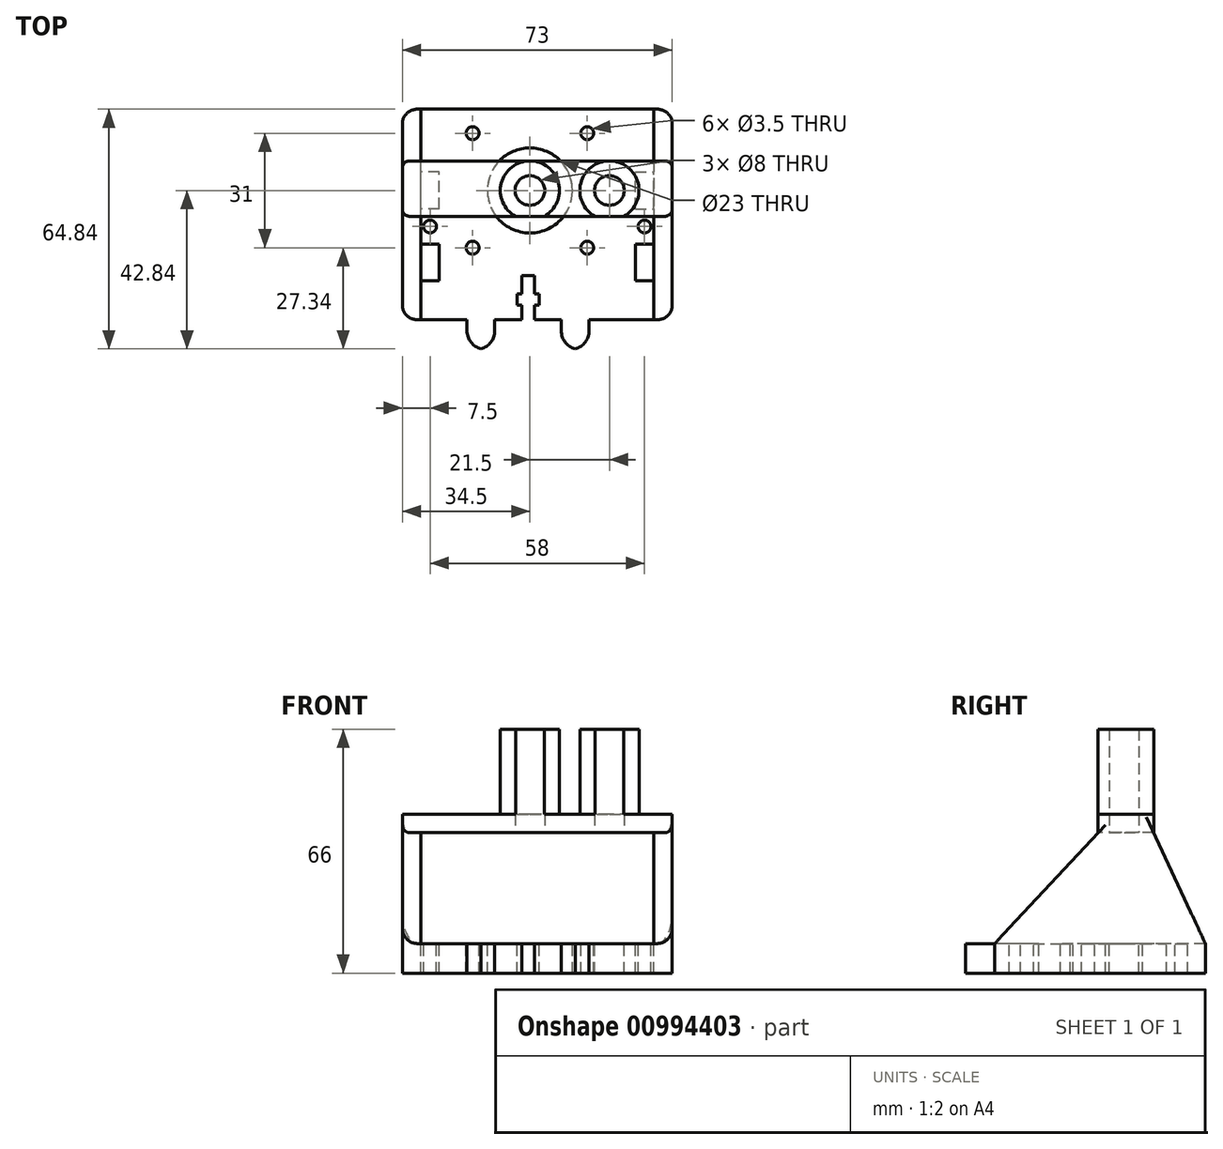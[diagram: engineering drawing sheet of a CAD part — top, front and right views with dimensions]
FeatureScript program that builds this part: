
annotation { "Feature Type Name" : "Feature", "Feature Type Description" : "" }
export const myFeature = defineFeature(function(context is Context, id is Id, definition is map)
    precondition{}
    {
        {
            var Q0;
            Q0=qCreatedBy(makeId("Top.planeOp"),FACE);
            var sketch = newSketch(context, id + "F0", { "sketchPlane" : qUnion([Q0])});
            skLineSegment(sketch, "E0.bottom", {"start": v(0, 0) * mm, "end": v(73, 0) * mm});
            skLineSegment(sketch, "E0.top", {"start": v(0, 57) * mm, "end": v(73, 57) * mm});
            skLineSegment(sketch, "E0.left", {"start": v(0, 0) * mm, "end": v(0, 57) * mm});
            skLineSegment(sketch, "E0.right", {"start": v(73, 0) * mm, "end": v(73, 57) * mm});
            skCircle(sketch, "E1", {"center": v(38.5, 35) * mm, "radius": 11.5 * mm});
            skCircle(sketch, "E2", {"center": v(17, 35) * mm, "radius": 4 * mm});
            skLineSegment(sketch, "E3.bottom", {"start": v(10, 10.5) * mm, "end": v(5, 10.5) * mm});
            skLineSegment(sketch, "E3.top", {"start": v(10, 20.5) * mm, "end": v(5, 20.5) * mm});
            skLineSegment(sketch, "E3.left", {"start": v(10, 10.5) * mm, "end": v(10, 20.5) * mm});
            skLineSegment(sketch, "E3.right", {"start": v(5, 10.5) * mm, "end": v(5, 20.5) * mm});
            skLineSegment(sketch, "E4.bottom", {"start": v(10, 30) * mm, "end": v(5, 30) * mm});
            skLineSegment(sketch, "E4.top", {"start": v(10, 40) * mm, "end": v(5, 40) * mm});
            skLineSegment(sketch, "E4.left", {"start": v(10, 30) * mm, "end": v(10, 40) * mm});
            skLineSegment(sketch, "E4.right", {"start": v(5, 30) * mm, "end": v(5, 40) * mm});
            skLineSegment(sketch, "E5.bottom", {"start": v(68, 10.5) * mm, "end": v(63, 10.5) * mm});
            skLineSegment(sketch, "E5.top", {"start": v(68, 20.5) * mm, "end": v(63, 20.5) * mm});
            skLineSegment(sketch, "E5.left", {"start": v(68, 10.5) * mm, "end": v(68, 20.5) * mm});
            skLineSegment(sketch, "E5.right", {"start": v(63, 10.5) * mm, "end": v(63, 20.5) * mm});
            skLineSegment(sketch, "E6.bottom", {"start": v(63, 30) * mm, "end": v(68, 30) * mm});
            skLineSegment(sketch, "E6.top", {"start": v(63, 40) * mm, "end": v(68, 40) * mm});
            skLineSegment(sketch, "E6.left", {"start": v(63, 30) * mm, "end": v(63, 40) * mm});
            skLineSegment(sketch, "E6.right", {"start": v(68, 30) * mm, "end": v(68, 40) * mm});
            skCircle(sketch, "E7", {"center": v(23, 50.5) * mm, "radius": 1.75 * mm});
            skCircle(sketch, "E8", {"center": v(54, 50.5) * mm, "radius": 1.75 * mm});
            skCircle(sketch, "E9", {"center": v(54, 19.5) * mm, "radius": 1.75 * mm});
            skCircle(sketch, "E10", {"center": v(23, 19.5) * mm, "radius": 1.75 * mm});
            skLineSegment(sketch, "E11", {"start": v(23, 50.5) * mm, "end": v(54, 19.5) * mm, "construction": true});
            skLineSegment(sketch, "E12", {"start": v(22.5, 0) * mm, "end": v(22.5, -8) * mm});
            skLineSegment(sketch, "E13", {"start": v(22.5, -8) * mm, "end": v(30, -8) * mm});
            skLineSegment(sketch, "E14", {"start": v(30, -8) * mm, "end": v(30, 0) * mm});
            skLineSegment(sketch, "E15", {"start": v(48, 0) * mm, "end": v(48, -8) * mm});
            skLineSegment(sketch, "E16", {"start": v(48, -8) * mm, "end": v(55.5, -8) * mm});
            skLineSegment(sketch, "E17", {"start": v(55.5, -8) * mm, "end": v(55.5, 0) * mm});
            skLineSegment(sketch, "E18", {"start": v(37.25, 0) * mm, "end": v(37.25, 12) * mm});
            skLineSegment(sketch, "E19", {"start": v(37.25, 12) * mm, "end": v(40.75, 12) * mm});
            skLineSegment(sketch, "E20", {"start": v(40.75, 12) * mm, "end": v(40.75, 0) * mm});
            skLineSegment(sketch, "E21.bottom", {"start": v(36, 7) * mm, "end": v(42, 7) * mm});
            skLineSegment(sketch, "E21.top", {"start": v(36, 4) * mm, "end": v(42, 4) * mm});
            skLineSegment(sketch, "E21.left", {"start": v(36, 7) * mm, "end": v(36, 4) * mm});
            skLineSegment(sketch, "E21.right", {"start": v(42, 7) * mm, "end": v(42, 4) * mm});
            skLineSegment(sketch, "E22", {"start": v(5, 30) * mm, "end": v(10, 20.5) * mm, "construction": true});
            skLineSegment(sketch, "E23", {"start": v(63, 30) * mm, "end": v(68, 20.5) * mm, "construction": true});
            skCircle(sketch, "E24", {"center": v(7.5, 25.25) * mm, "radius": 1.75 * mm});
            skCircle(sketch, "E25", {"center": v(65.5, 25.25) * mm, "radius": 1.75 * mm});
            skSolve(sketch);
        }
        {
            var Q0;
            Q0=makeQuery(id+"F0.imprint","IMPRINT",FACE,{"disambiguationData":[TD([[makeQuery(id+"F0.imprint","IMPRINT",EDGE,{"derivedFrom":sQuery(id+"F0.wireOp",EDGE,"E0.top")}),-1.0]])]});
            var Q1;
            {var subQ0=sQuery(id+"F0.wireOp",EDGE,"E15");Q1=makeQuery(id+"F0.imprint","IMPRINT",FACE,{"disambiguationData":[TD([[makeQuery(id+"F0.imprint","IMPRINT",EDGE,{"derivedFrom":subQ0}),1.0]])]});}
            var Q2;
            {var subQ0=sQuery(id+"F0.wireOp",EDGE,"E12");Q2=makeQuery(id+"F0.imprint","IMPRINT",FACE,{"disambiguationData":[TD([[makeQuery(id+"F0.imprint","IMPRINT",EDGE,{"derivedFrom":subQ0}),1.0]])]});}
            extrude(context, id + "F1", {"entities" : qUnion([Q0, Q1, Q2]), "oppositeDirection" : true, "depth" : 8 * mm, "offsetDistance" : 25 * mm});
        }
        {
            var Q0;
            Q0=qCreatedBy(makeId("Top.planeOp"),FACE);
            var sketch = newSketch(context, id + "F2", { "sketchPlane" : qUnion([Q0])});
            skLineSegment(sketch, "E26.0.0", {"start": v(0, 0) * mm, "end": v(22.5, 0) * mm});
            skLineSegment(sketch, "E26.0.1", {"start": v(22.5, 0) * mm, "end": v(22.5, -8) * mm});
            skLineSegment(sketch, "E26.0.2", {"start": v(22.5, -8) * mm, "end": v(30, -8) * mm});
            skLineSegment(sketch, "E26.0.3", {"start": v(30, -8) * mm, "end": v(30, 0) * mm});
            skLineSegment(sketch, "E26.0.4", {"start": v(30, 0) * mm, "end": v(37.25, 0) * mm});
            skLineSegment(sketch, "E26.0.5", {"start": v(37.25, 0) * mm, "end": v(37.25, 4) * mm});
            skLineSegment(sketch, "E26.0.6", {"start": v(37.25, 4) * mm, "end": v(36, 4) * mm});
            skLineSegment(sketch, "E26.0.7", {"start": v(36, 4) * mm, "end": v(36, 7) * mm});
            skLineSegment(sketch, "E26.0.8", {"start": v(36, 7) * mm, "end": v(37.25, 7) * mm});
            skLineSegment(sketch, "E26.0.9", {"start": v(37.25, 7) * mm, "end": v(37.25, 12) * mm});
            skLineSegment(sketch, "E26.0.10", {"start": v(37.25, 12) * mm, "end": v(40.75, 12) * mm});
            skLineSegment(sketch, "E26.0.11", {"start": v(40.75, 12) * mm, "end": v(40.75, 7) * mm});
            skLineSegment(sketch, "E26.0.12", {"start": v(40.75, 7) * mm, "end": v(42, 7) * mm});
            skLineSegment(sketch, "E26.0.13", {"start": v(42, 7) * mm, "end": v(42, 4) * mm});
            skLineSegment(sketch, "E26.0.14", {"start": v(42, 4) * mm, "end": v(40.75, 4) * mm});
            skLineSegment(sketch, "E26.0.15", {"start": v(40.75, 4) * mm, "end": v(40.75, 0) * mm});
            skLineSegment(sketch, "E26.0.16", {"start": v(40.75, 0) * mm, "end": v(48, 0) * mm});
            skLineSegment(sketch, "E26.0.17", {"start": v(48, 0) * mm, "end": v(48, -8) * mm});
            skLineSegment(sketch, "E26.0.18", {"start": v(48, -8) * mm, "end": v(55.5, -8) * mm});
            skLineSegment(sketch, "E26.0.19", {"start": v(55.5, -8) * mm, "end": v(55.5, 0) * mm});
            skLineSegment(sketch, "E26.0.20", {"start": v(55.5, 0) * mm, "end": v(73, 0) * mm});
            skLineSegment(sketch, "E26.0.21", {"start": v(73, 0) * mm, "end": v(73, 57) * mm});
            skLineSegment(sketch, "E26.0.22", {"start": v(73, 57) * mm, "end": v(0, 57) * mm});
            skLineSegment(sketch, "E26.0.23", {"start": v(0, 57) * mm, "end": v(0, 0) * mm});
            skLineSegment(sketch, "E27.0.0", {"start": v(5, 30) * mm, "end": v(10, 30) * mm});
            skLineSegment(sketch, "E27.0.1", {"start": v(10, 30) * mm, "end": v(10, 40) * mm});
            skLineSegment(sketch, "E27.0.2", {"start": v(10, 40) * mm, "end": v(5, 40) * mm});
            skLineSegment(sketch, "E27.0.3", {"start": v(5, 40) * mm, "end": v(5, 30) * mm});
            skLineSegment(sketch, "E28.0.0", {"start": v(5, 10.5) * mm, "end": v(10, 10.5) * mm});
            skLineSegment(sketch, "E28.0.1", {"start": v(10, 10.5) * mm, "end": v(10, 20.5) * mm});
            skLineSegment(sketch, "E28.0.2", {"start": v(10, 20.5) * mm, "end": v(5, 20.5) * mm});
            skLineSegment(sketch, "E28.0.3", {"start": v(5, 20.5) * mm, "end": v(5, 10.5) * mm});
            skCircle(sketch, "E29.0.0", {"center": v(7.5, 25.25) * mm, "radius": 1.75 * mm});
            skLineSegment(sketch, "E30.0.0", {"start": v(63, 10.5) * mm, "end": v(68, 10.5) * mm});
            skLineSegment(sketch, "E30.0.1", {"start": v(68, 10.5) * mm, "end": v(68, 20.5) * mm});
            skLineSegment(sketch, "E30.0.2", {"start": v(68, 20.5) * mm, "end": v(63, 20.5) * mm});
            skLineSegment(sketch, "E30.0.3", {"start": v(63, 20.5) * mm, "end": v(63, 10.5) * mm});
            skCircle(sketch, "E31.0.0", {"center": v(65.5, 25.25) * mm, "radius": 1.75 * mm});
            skLineSegment(sketch, "E32.0.0", {"start": v(63, 40) * mm, "end": v(63, 30) * mm});
            skLineSegment(sketch, "E32.0.1", {"start": v(63, 30) * mm, "end": v(68, 30) * mm});
            skLineSegment(sketch, "E32.0.2", {"start": v(68, 30) * mm, "end": v(68, 40) * mm});
            skLineSegment(sketch, "E32.0.3", {"start": v(68, 40) * mm, "end": v(63, 40) * mm});
            skPoint(sketch, "E33.0", {"position": v(17, 35) * mm});
            skLineSegment(sketch, "E34", {"start": v(5, 57) * mm, "end": v(5, 0) * mm});
            skLineSegment(sketch, "E35", {"start": v(68, 0) * mm, "end": v(68, 57) * mm});
            skSolve(sketch);
        }
        {
            var Q0;
            {var subQ0=sQuery(id+"F2.wireOp",EDGE,"E26.0.23");Q0=makeQuery(id+"F2.imprint","IMPRINT",FACE,{"disambiguationData":[TD([[makeQuery(id+"F2.imprint","IMPRINT",EDGE,{"derivedFrom":subQ0}),1.0]])]});}
            var Q1;
            {var subQ1=sQuery(id+"F2.wireOp",EDGE,"E26.0.21");Q1=makeQuery(id+"F2.imprint","IMPRINT",FACE,{"disambiguationData":[TD([[makeQuery(id+"F2.imprint","IMPRINT",EDGE,{"derivedFrom":subQ1}),1.0]])]});}
            extrude(context, id + "F3", {"entities" : qUnion([Q0, Q1]), "operationType" : NewBodyOperationType.ADD, "depth" : 30 * mm, "offsetDistance" : 25 * mm});
        }
        {
            var Q0;
            Q0=makeQuery(id+"F3.opExtrude","CAP_FACE",FACE,{"disambiguationData":[OSD([sQuery(id+"F2.wireOp",EDGE,"E26.0.0"),sQuery(id+"F2.wireOp",EDGE,"E26.0.22"),sQuery(id+"F2.wireOp",EDGE,"E26.0.23"),sQuery(id+"F2.wireOp",EDGE,"E27.0.3"),sQuery(id+"F2.wireOp",EDGE,"E28.0.3"),sQuery(id+"F2.wireOp",EDGE,"E34")])],"isStart":false});
            var sketch = newSketch(context, id + "F4", { "sketchPlane" : qUnion([Q0])});
            skLineSegment(sketch, "E36.0.0", {"start": v(0, 57) * mm, "end": v(0, 0) * mm});
            skLineSegment(sketch, "E36.0.1", {"start": v(0, 0) * mm, "end": v(5, 0) * mm});
            skLineSegment(sketch, "E36.0.2", {"start": v(5, 0) * mm, "end": v(5, 57) * mm});
            skLineSegment(sketch, "E36.0.3", {"start": v(5, 57) * mm, "end": v(0, 57) * mm});
            skLineSegment(sketch, "E37.0.0", {"start": v(68, 57) * mm, "end": v(68, 0) * mm});
            skLineSegment(sketch, "E37.0.1", {"start": v(68, 0) * mm, "end": v(73, 0) * mm});
            skLineSegment(sketch, "E37.0.2", {"start": v(73, 0) * mm, "end": v(73, 57) * mm});
            skLineSegment(sketch, "E37.0.3", {"start": v(73, 57) * mm, "end": v(68, 57) * mm});
            skCircle(sketch, "E38.0", {"center": v(17, 35) * mm, "radius": 4 * mm});
            skLineSegment(sketch, "E39", {"start": v(0, 43) * mm, "end": v(73, 43) * mm});
            skLineSegment(sketch, "E40", {"start": v(73, 28) * mm, "end": v(0, 28) * mm});
            skPoint(sketch, "E41.0", {"position": v(38.5, 35) * mm});
            skCircle(sketch, "E42", {"center": v(38.5, 35) * mm, "radius": 4 * mm});
            skSolve(sketch);
        }
        {
            var Q0;
            {var subQ0=sQuery(id+"F4.wireOp",EDGE,"E40");var subQ1=sQuery(id+"F4.wireOp",EDGE,"E36.0.0");var subQ2=makeQuery(id+"F4.imprint","INTERSECT",VERTEX,{"derivedFrom":[subQ1,subQ0]});Q0=makeQuery(id+"F4.imprint","IMPRINT",FACE,{"disambiguationData":[TD([[makeQuery(id+"F4.imprint","IMPRINT",EDGE,{"disambiguationData":[TD([[subQ2,1.0]])],"derivedFrom":subQ1}),1.0]])]});}
            var Q1;
            Q1=makeQuery(id+"F4.imprint","IMPRINT",FACE,{"disambiguationData":[TD([[makeQuery(id+"F4.imprint","IMPRINT",EDGE,{"derivedFrom":sQuery(id+"F4.wireOp",EDGE,"E38.0")}),-1.0]])]});
            var Q2;
            {var subQ0=sQuery(id+"F4.wireOp",EDGE,"E40");var subQ1=sQuery(id+"F4.wireOp",EDGE,"E37.0.0");var subQ2=makeQuery(id+"F4.imprint","INTERSECT",VERTEX,{"derivedFrom":[subQ1,subQ0]});Q2=makeQuery(id+"F4.imprint","IMPRINT",FACE,{"disambiguationData":[TD([[makeQuery(id+"F4.imprint","IMPRINT",EDGE,{"disambiguationData":[TD([[subQ2,1.0]])],"derivedFrom":subQ1}),1.0]])]});}
            extrude(context, id + "F5", {"entities" : qUnion([Q0, Q1, Q2]), "operationType" : NewBodyOperationType.ADD, "depth" : 5 * mm, "offsetDistance" : 25 * mm});
        }
        {
            var Q0;
            Q0=makeQuery(id+"F5.opExtrude","CAP_FACE",FACE,{"disambiguationData":[OSD([sQuery(id+"F4.wireOp",EDGE,"E36.0.0"),sQuery(id+"F4.wireOp",EDGE,"E37.0.2"),sQuery(id+"F4.wireOp",EDGE,"E38.0"),sQuery(id+"F4.wireOp",EDGE,"E39"),sQuery(id+"F4.wireOp",EDGE,"E40"),sQuery(id+"F4.wireOp",EDGE,"E42")])],"isStart":false});
            var sketch = newSketch(context, id + "F6", { "sketchPlane" : qUnion([Q0])});
            skLineSegment(sketch, "E43.0.0", {"start": v(73, 43) * mm, "end": v(0, 43) * mm});
            skLineSegment(sketch, "E43.0.1", {"start": v(0, 43) * mm, "end": v(0, 28) * mm});
            skLineSegment(sketch, "E43.0.2", {"start": v(0, 28) * mm, "end": v(73, 28) * mm});
            skLineSegment(sketch, "E43.0.3", {"start": v(73, 28) * mm, "end": v(73, 43) * mm});
            skCircle(sketch, "E44.0.0", {"center": v(17, 35) * mm, "radius": 4 * mm});
            skCircle(sketch, "E45.0", {"center": v(38.5, 35) * mm, "radius": 4 * mm});
            skCircle(sketch, "E46", {"center": v(17, 35) * mm, "radius": 8 * mm});
            skCircle(sketch, "E47", {"center": v(38.5, 35) * mm, "radius": 8 * mm});
            skSolve(sketch);
        }
        {
            var Q0;
            Q0=makeQuery(id+"F6.imprint","IMPRINT",FACE,{"disambiguationData":[TD([[makeQuery(id+"F6.imprint","IMPRINT",EDGE,{"derivedFrom":sQuery(id+"F6.wireOp",EDGE,"E44.0.0")}),-1.0]])]});
            var Q1;
            Q1=makeQuery(id+"F6.imprint","IMPRINT",FACE,{"disambiguationData":[TD([[makeQuery(id+"F6.imprint","IMPRINT",EDGE,{"derivedFrom":sQuery(id+"F6.wireOp",EDGE,"E45.0")}),-1.0]])]});
            extrude(context, id + "F7", {"entities" : qUnion([Q0, Q1]), "operationType" : NewBodyOperationType.ADD, "depth" : 23 * mm, "offsetDistance" : 25 * mm});
        }
        {
            var Q0;
            Q0=makeQuery(id+"F5.boolean.opBoolean","MERGE",FACE,{"derivedFrom":[makeQuery(id+"F3.boolean.opBoolean","MERGE",FACE,{"derivedFrom":[makeQuery(id+"F1.opExtrude","SWEPT_FACE",FACE,{"disambiguationData":[OSD([sQuery(id+"F0.wireOp",EDGE,"E0.left")])]}),makeQuery(id+"F3.opExtrude","SWEPT_FACE",FACE,{"disambiguationData":[OSD([sQuery(id+"F2.wireOp",EDGE,"E26.0.23")])]})]}),makeQuery(id+"F5.opExtrude","SWEPT_FACE",FACE,{"disambiguationData":[OSD([sQuery(id+"F4.wireOp",EDGE,"E36.0.0")])]})]});
            var sketch = newSketch(context, id + "F8", { "sketchPlane" : qUnion([Q0])});
            skPoint(sketch, "E48.0", {"position": v(-28, 30) * mm});
            skPoint(sketch, "E49.0", {"position": v(-57, 0) * mm});
            skPoint(sketch, "E50.0", {"position": v(-43, 30) * mm});
            skLineSegment(sketch, "E51", {"start": v(-28, 30) * mm, "end": v(0, 0) * mm});
            skLineSegment(sketch, "E52", {"start": v(-43, 30) * mm, "end": v(-57, 0) * mm});
            skSolve(sketch);
        }
        {
            var Q0;
            {var subQ0=sQuery(id+"F8.wireOp",EDGE,"E52");Q0=makeQuery(id+"F8.imprint","IMPRINT",FACE,{"disambiguationData":[TD([[makeQuery(id+"F8.imprint","IMPRINT",EDGE,{"derivedFrom":subQ0}),-1.0]])]});}
            var Q1;
            {var subQ0=sQuery(id+"F8.wireOp",EDGE,"E51");Q1=makeQuery(id+"F8.imprint","IMPRINT",FACE,{"disambiguationData":[TD([[makeQuery(id+"F8.imprint","IMPRINT",EDGE,{"derivedFrom":subQ0}),1.0]])]});}
            extrude(context, id + "F9", {"entities" : qUnion([Q0, Q1]), "operationType" : NewBodyOperationType.REMOVE, "oppositeDirection" : true, "depth" : 73 * mm, "offsetDistance" : 25 * mm});
        }
        {
            var Q0;
            Q0=makeQuery(id+"F3.boolean.opBoolean","MERGE",EDGE,{"derivedFrom":[makeQuery(id+"F1.opExtrude","SWEPT_EDGE",EDGE,{"disambiguationData":[OSD([sQuery(id+"F0.wireOp",EDGE,"E0.top"),sQuery(id+"F0.wireOp",EDGE,"E0.left")])]}),makeQuery(id+"F3.opExtrude","SWEPT_EDGE",EDGE,{"disambiguationData":[OSD([sQuery(id+"F2.wireOp",EDGE,"E26.0.22"),sQuery(id+"F2.wireOp",EDGE,"E26.0.23")])]})]});
            var Q1;
            Q1=makeQuery(id+"F3.boolean.opBoolean","MERGE",EDGE,{"derivedFrom":[makeQuery(id+"F1.opExtrude","SWEPT_EDGE",EDGE,{"disambiguationData":[OSD([sQuery(id+"F0.wireOp",EDGE,"E0.top"),sQuery(id+"F0.wireOp",EDGE,"E0.right")])]}),makeQuery(id+"F3.opExtrude","SWEPT_EDGE",EDGE,{"disambiguationData":[OSD([sQuery(id+"F2.wireOp",EDGE,"E26.0.21"),sQuery(id+"F2.wireOp",EDGE,"E26.0.22")])]})]});
            var Q2;
            Q2=makeQuery(id+"F3.boolean.opBoolean","MERGE",EDGE,{"derivedFrom":[makeQuery(id+"F1.opExtrude","SWEPT_EDGE",EDGE,{"disambiguationData":[OSD([sQuery(id+"F0.wireOp",EDGE,"E0.bottom"),sQuery(id+"F0.wireOp",EDGE,"E0.left")])]}),makeQuery(id+"F3.opExtrude","SWEPT_EDGE",EDGE,{"disambiguationData":[OSD([sQuery(id+"F2.wireOp",EDGE,"E26.0.0"),sQuery(id+"F2.wireOp",EDGE,"E26.0.23")])]})]});
            var Q3;
            Q3=makeQuery(id+"F3.boolean.opBoolean","MERGE",EDGE,{"derivedFrom":[makeQuery(id+"F1.opExtrude","SWEPT_EDGE",EDGE,{"disambiguationData":[OSD([sQuery(id+"F0.wireOp",EDGE,"E0.bottom"),sQuery(id+"F0.wireOp",EDGE,"E0.right")])]}),makeQuery(id+"F3.opExtrude","SWEPT_EDGE",EDGE,{"disambiguationData":[OSD([sQuery(id+"F2.wireOp",EDGE,"E26.0.20"),sQuery(id+"F2.wireOp",EDGE,"E26.0.21")])]})]});
            fillet(context, id + "F10", {"entities" : qUnion([Q0, Q1, Q2, Q3]), "tangentPropagation" : true, "radius" : 4 * mm, "defaultsChanged" : true, "vertexSettings" : [], "allowEdgeOverflow" : false});
        }
        {
            var Q0;
            Q0=makeQuery(id+"F5.opExtrude","SWEPT_EDGE",EDGE,{"disambiguationData":[OSD([sQuery(id+"F4.wireOp",EDGE,"E37.0.2"),sQuery(id+"F4.wireOp",EDGE,"E40")])]});
            var Q1;
            Q1=makeQuery(id+"F5.opExtrude","SWEPT_EDGE",EDGE,{"disambiguationData":[OSD([sQuery(id+"F4.wireOp",EDGE,"E36.0.0"),sQuery(id+"F4.wireOp",EDGE,"E40")])]});
            var Q2;
            Q2=makeQuery(id+"F5.opExtrude","SWEPT_EDGE",EDGE,{"disambiguationData":[OSD([sQuery(id+"F4.wireOp",EDGE,"E36.0.0"),sQuery(id+"F4.wireOp",EDGE,"E39")])]});
            var Q3;
            Q3=makeQuery(id+"F5.opExtrude","SWEPT_EDGE",EDGE,{"disambiguationData":[OSD([sQuery(id+"F4.wireOp",EDGE,"E37.0.2"),sQuery(id+"F4.wireOp",EDGE,"E39")])]});
            fillet(context, id + "F11", {"entities" : qUnion([Q0, Q1, Q2, Q3]), "tangentPropagation" : true, "radius" : 2 * mm, "defaultsChanged" : true, "vertexSettings" : [], "allowEdgeOverflow" : false});
        }
        {
            var Q0;
            Q0=makeQuery(id+"F1.opExtrude","SWEPT_EDGE",EDGE,{"disambiguationData":[OSD([sQuery(id+"F0.wireOp",EDGE,"E13"),sQuery(id+"F0.wireOp",EDGE,"E14")])]});
            var Q1;
            Q1=makeQuery(id+"F1.opExtrude","SWEPT_EDGE",EDGE,{"disambiguationData":[OSD([sQuery(id+"F0.wireOp",EDGE,"E12"),sQuery(id+"F0.wireOp",EDGE,"E13")])]});
            var Q2;
            Q2=makeQuery(id+"F1.opExtrude","SWEPT_EDGE",EDGE,{"disambiguationData":[OSD([sQuery(id+"F0.wireOp",EDGE,"E16"),sQuery(id+"F0.wireOp",EDGE,"E17")])]});
            var Q3;
            Q3=makeQuery(id+"F1.opExtrude","SWEPT_EDGE",EDGE,{"disambiguationData":[OSD([sQuery(id+"F0.wireOp",EDGE,"E15"),sQuery(id+"F0.wireOp",EDGE,"E16")])]});
            fillet(context, id + "F12", {"entities" : qUnion([Q0, Q1, Q2, Q3]), "tangentPropagation" : true, "radius" : 5 * mm, "defaultsChanged" : false, "vertexSettings" : [], "allowEdgeOverflow" : false});
        }
        {
            var Q0;
            Q0=makeQuery(id+"F1.opExtrude","SWEPT_BODY",BODY,{"disambiguationData":[OSD([sQuery(id+"F0.wireOp",EDGE,"E0.bottom"),sQuery(id+"F0.wireOp",EDGE,"E0.top"),sQuery(id+"F0.wireOp",EDGE,"E0.left"),sQuery(id+"F0.wireOp",EDGE,"E0.right"),sQuery(id+"F0.wireOp",EDGE,"E1"),sQuery(id+"F0.wireOp",EDGE,"E2"),sQuery(id+"F0.wireOp",EDGE,"E3.bottom"),sQuery(id+"F0.wireOp",EDGE,"E3.top"),sQuery(id+"F0.wireOp",EDGE,"E3.left"),sQuery(id+"F0.wireOp",EDGE,"E3.right"),sQuery(id+"F0.wireOp",EDGE,"E4.bottom"),sQuery(id+"F0.wireOp",EDGE,"E4.top"),sQuery(id+"F0.wireOp",EDGE,"E4.left"),sQuery(id+"F0.wireOp",EDGE,"E4.right"),sQuery(id+"F0.wireOp",EDGE,"E5.bottom"),sQuery(id+"F0.wireOp",EDGE,"E5.top"),sQuery(id+"F0.wireOp",EDGE,"E5.left"),sQuery(id+"F0.wireOp",EDGE,"E5.right"),sQuery(id+"F0.wireOp",EDGE,"E6.bottom"),sQuery(id+"F0.wireOp",EDGE,"E6.top"),sQuery(id+"F0.wireOp",EDGE,"E6.left"),sQuery(id+"F0.wireOp",EDGE,"E6.right"),sQuery(id+"F0.wireOp",EDGE,"E7"),sQuery(id+"F0.wireOp",EDGE,"E8"),sQuery(id+"F0.wireOp",EDGE,"E9"),sQuery(id+"F0.wireOp",EDGE,"E10"),sQuery(id+"F0.wireOp",EDGE,"E12"),sQuery(id+"F0.wireOp",EDGE,"E13"),sQuery(id+"F0.wireOp",EDGE,"E14"),sQuery(id+"F0.wireOp",EDGE,"E15"),sQuery(id+"F0.wireOp",EDGE,"E16"),sQuery(id+"F0.wireOp",EDGE,"E17"),sQuery(id+"F0.wireOp",EDGE,"E18"),sQuery(id+"F0.wireOp",EDGE,"E19"),sQuery(id+"F0.wireOp",EDGE,"E20"),sQuery(id+"F0.wireOp",EDGE,"E21.bottom"),sQuery(id+"F0.wireOp",EDGE,"E21.top"),sQuery(id+"F0.wireOp",EDGE,"E21.left"),sQuery(id+"F0.wireOp",EDGE,"E21.right"),sQuery(id+"F0.wireOp",EDGE,"E24"),sQuery(id+"F0.wireOp",EDGE,"E25")])]});
            var Q1;
            Q1=makeQuery(id+"F5.boolean.opBoolean","MERGE",FACE,{"derivedFrom":[makeQuery(id+"F3.boolean.opBoolean","MERGE",FACE,{"derivedFrom":[makeQuery(id+"F1.opExtrude","SWEPT_FACE",FACE,{"disambiguationData":[OSD([sQuery(id+"F0.wireOp",EDGE,"E0.left")])]}),makeQuery(id+"F3.opExtrude","SWEPT_FACE",FACE,{"disambiguationData":[OSD([sQuery(id+"F2.wireOp",EDGE,"E26.0.23")])]})]}),makeQuery(id+"F5.opExtrude","SWEPT_FACE",FACE,{"disambiguationData":[OSD([sQuery(id+"F4.wireOp",EDGE,"E36.0.0")])]})]});
            mirror(context, id + "F13", {"entities" : qUnion([Q0]), "mirrorPlane" : qUnion([Q1])});
        }
        {
            var Q0;
            Q0=makeQuery(id+"F1.opExtrude","SWEPT_BODY",BODY,{"disambiguationData":[OSD([sQuery(id+"F0.wireOp",EDGE,"E0.bottom"),sQuery(id+"F0.wireOp",EDGE,"E0.top"),sQuery(id+"F0.wireOp",EDGE,"E0.left"),sQuery(id+"F0.wireOp",EDGE,"E0.right"),sQuery(id+"F0.wireOp",EDGE,"E1"),sQuery(id+"F0.wireOp",EDGE,"E2"),sQuery(id+"F0.wireOp",EDGE,"E3.bottom"),sQuery(id+"F0.wireOp",EDGE,"E3.top"),sQuery(id+"F0.wireOp",EDGE,"E3.left"),sQuery(id+"F0.wireOp",EDGE,"E3.right"),sQuery(id+"F0.wireOp",EDGE,"E4.bottom"),sQuery(id+"F0.wireOp",EDGE,"E4.top"),sQuery(id+"F0.wireOp",EDGE,"E4.left"),sQuery(id+"F0.wireOp",EDGE,"E4.right"),sQuery(id+"F0.wireOp",EDGE,"E5.bottom"),sQuery(id+"F0.wireOp",EDGE,"E5.top"),sQuery(id+"F0.wireOp",EDGE,"E5.left"),sQuery(id+"F0.wireOp",EDGE,"E5.right"),sQuery(id+"F0.wireOp",EDGE,"E6.bottom"),sQuery(id+"F0.wireOp",EDGE,"E6.top"),sQuery(id+"F0.wireOp",EDGE,"E6.left"),sQuery(id+"F0.wireOp",EDGE,"E6.right"),sQuery(id+"F0.wireOp",EDGE,"E7"),sQuery(id+"F0.wireOp",EDGE,"E8"),sQuery(id+"F0.wireOp",EDGE,"E9"),sQuery(id+"F0.wireOp",EDGE,"E10"),sQuery(id+"F0.wireOp",EDGE,"E12"),sQuery(id+"F0.wireOp",EDGE,"E13"),sQuery(id+"F0.wireOp",EDGE,"E14"),sQuery(id+"F0.wireOp",EDGE,"E15"),sQuery(id+"F0.wireOp",EDGE,"E16"),sQuery(id+"F0.wireOp",EDGE,"E17"),sQuery(id+"F0.wireOp",EDGE,"E18"),sQuery(id+"F0.wireOp",EDGE,"E19"),sQuery(id+"F0.wireOp",EDGE,"E20"),sQuery(id+"F0.wireOp",EDGE,"E21.bottom"),sQuery(id+"F0.wireOp",EDGE,"E21.top"),sQuery(id+"F0.wireOp",EDGE,"E21.left"),sQuery(id+"F0.wireOp",EDGE,"E21.right"),sQuery(id+"F0.wireOp",EDGE,"E24"),sQuery(id+"F0.wireOp",EDGE,"E25")])]});
            deleteBodies(context, id + "F14", {"entities" : qUnion([Q0])});
        }
    });
